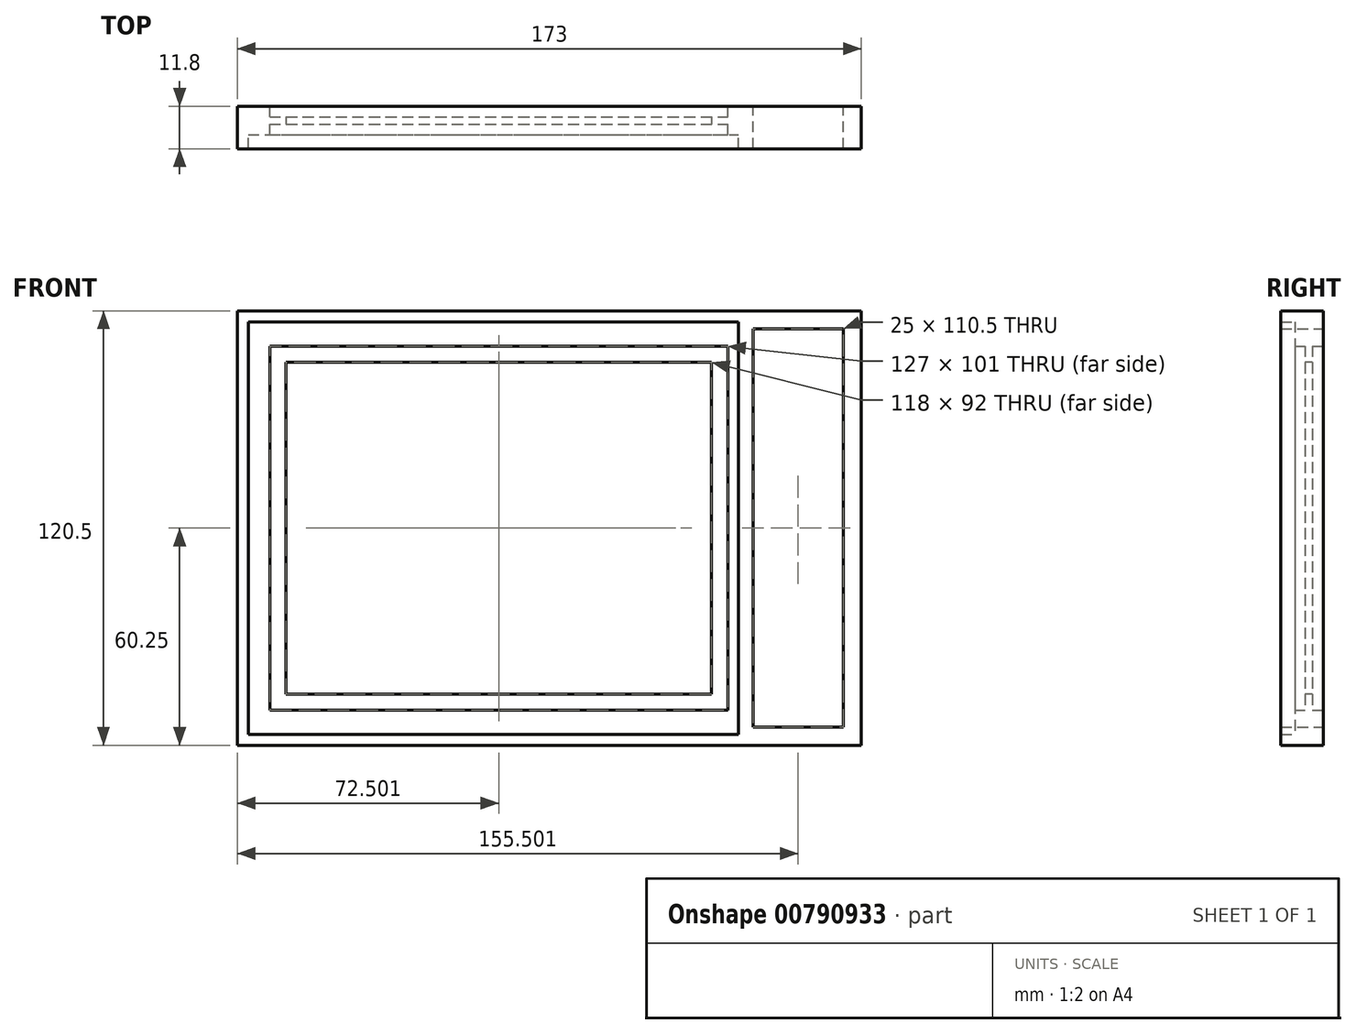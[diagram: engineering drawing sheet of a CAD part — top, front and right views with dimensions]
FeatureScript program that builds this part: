
annotation { "Feature Type Name" : "Feature", "Feature Type Description" : "" }
export const myFeature = defineFeature(function(context is Context, id is Id, definition is map)
    precondition{}
    {
        {
            var Q0;
            Q0=qCreatedBy(makeId("Front.planeOp"),FACE);
            var sketch = newSketch(context, id + "F0", { "sketchPlane" : qUnion([Q0])});
            skLineSegment(sketch, "E0.bottom", {"start": v(-104.32, 60.25) * mm, "end": v(68.68, 60.25) * mm});
            skLineSegment(sketch, "E0.top", {"start": v(-104.32, -60.25) * mm, "end": v(68.68, -60.25) * mm});
            skLineSegment(sketch, "E0.left", {"start": v(-104.32, 60.25) * mm, "end": v(-104.32, -60.25) * mm});
            skLineSegment(sketch, "E0.right", {"start": v(68.68, 60.25) * mm, "end": v(68.68, -60.25) * mm});
            skLineSegment(sketch, "E1.bottom", {"start": v(-95.32, 50.5) * mm, "end": v(31.68, 50.5) * mm});
            skLineSegment(sketch, "E1.top", {"start": v(-95.32, -50.5) * mm, "end": v(31.68, -50.5) * mm});
            skLineSegment(sketch, "E1.left", {"start": v(-95.32, 50.5) * mm, "end": v(-95.32, -50.5) * mm});
            skLineSegment(sketch, "E1.right", {"start": v(31.68, 50.5) * mm, "end": v(31.68, -50.5) * mm});
            skLineSegment(sketch, "E2.bottom", {"start": v(38.68, 55.25) * mm, "end": v(63.68, 55.25) * mm});
            skLineSegment(sketch, "E2.top", {"start": v(38.68, -55.25) * mm, "end": v(63.68, -55.25) * mm});
            skLineSegment(sketch, "E2.left", {"start": v(38.68, 55.25) * mm, "end": v(38.68, -55.25) * mm});
            skLineSegment(sketch, "E2.right", {"start": v(63.68, 55.25) * mm, "end": v(63.68, -55.25) * mm});
            skLineSegment(sketch, "E3.bottom", {"start": v(-90.82, 46) * mm, "end": v(27.18, 46) * mm});
            skLineSegment(sketch, "E3.top", {"start": v(-90.82, -46) * mm, "end": v(27.18, -46) * mm});
            skLineSegment(sketch, "E3.left", {"start": v(-90.82, 46) * mm, "end": v(-90.82, -46) * mm});
            skLineSegment(sketch, "E3.right", {"start": v(27.18, 46) * mm, "end": v(27.18, -46) * mm});
            skLineSegment(sketch, "E4.bottom", {"start": v(-101.32, 57.25) * mm, "end": v(34.68, 57.25) * mm});
            skLineSegment(sketch, "E4.top", {"start": v(-101.32, -57.25) * mm, "end": v(34.68, -57.25) * mm});
            skLineSegment(sketch, "E4.left", {"start": v(-101.32, 57.25) * mm, "end": v(-101.32, -57.25) * mm});
            skLineSegment(sketch, "E4.right", {"start": v(34.68, 57.25) * mm, "end": v(34.68, -57.25) * mm});
            skSolve(sketch);
        }
        {
            var Q0;
            Q0=qSketchRegion(id+"F0",true);
            var Q1;
            Q1=makeQuery(id+"F0.imprint","IMPRINT",FACE,{"disambiguationData":[TD([[makeQuery(id+"F0.imprint","IMPRINT",EDGE,{"derivedFrom":sQuery(id+"F0.wireOp",EDGE,"E1.bottom")}),1.0]])]});
            extrude(context, id + "F1", {"entities" : qUnion([Q0, Q1]), "depth" : 5.9 * mm, "offsetDistance" : 25 * mm});
        }
        {
            var Q0;
            Q0=makeQuery(id+"F1.opExtrude","SWEPT_BODY",BODY,{"disambiguationData":[OSD([sQuery(id+"F0.wireOp",EDGE,"E0.bottom"),sQuery(id+"F0.wireOp",EDGE,"E0.top"),sQuery(id+"F0.wireOp",EDGE,"E0.left"),sQuery(id+"F0.wireOp",EDGE,"E0.right"),sQuery(id+"F0.wireOp",EDGE,"E1.bottom"),sQuery(id+"F0.wireOp",EDGE,"E1.top"),sQuery(id+"F0.wireOp",EDGE,"E1.left"),sQuery(id+"F0.wireOp",EDGE,"E1.right"),sQuery(id+"F0.wireOp",EDGE,"E2.top"),sQuery(id+"F0.wireOp",EDGE,"E2.left"),sQuery(id+"F0.wireOp",EDGE,"E2.right")])]});
            var Q1;
            Q1=makeQuery(id+"F1.opExtrude","CAP_FACE",FACE,{"disambiguationData":[OSD([sQuery(id+"F0.wireOp",EDGE,"E0.bottom"),sQuery(id+"F0.wireOp",EDGE,"E0.top"),sQuery(id+"F0.wireOp",EDGE,"E0.left"),sQuery(id+"F0.wireOp",EDGE,"E0.right"),sQuery(id+"F0.wireOp",EDGE,"E1.bottom"),sQuery(id+"F0.wireOp",EDGE,"E1.top"),sQuery(id+"F0.wireOp",EDGE,"E1.left"),sQuery(id+"F0.wireOp",EDGE,"E1.right"),sQuery(id+"F0.wireOp",EDGE,"E2.bottom"),sQuery(id+"F0.wireOp",EDGE,"E2.left"),sQuery(id+"F0.wireOp",EDGE,"E2.right")])],"isStart":true});
            mirror(context, id + "F2", {"operationType" : NewBodyOperationType.ADD, "entities" : qUnion([Q0]), "mirrorPlane" : qUnion([Q1])});
        }
        {
            var Q0;
            Q0=makeQuery(id+"F0.imprint","IMPRINT",FACE,{"disambiguationData":[TD([[makeQuery(id+"F0.imprint","IMPRINT",EDGE,{"derivedFrom":sQuery(id+"F0.wireOp",EDGE,"E1.bottom")}),-1.0]])]});
            var Q1;
            Q1=makeQuery(id+"F1.opExtrude","CAP_FACE",FACE,{"disambiguationData":[OSD([sQuery(id+"F0.wireOp",EDGE,"E0.bottom"),sQuery(id+"F0.wireOp",EDGE,"E0.top"),sQuery(id+"F0.wireOp",EDGE,"E0.left"),sQuery(id+"F0.wireOp",EDGE,"E0.right"),sQuery(id+"F0.wireOp",EDGE,"E1.bottom"),sQuery(id+"F0.wireOp",EDGE,"E1.top"),sQuery(id+"F0.wireOp",EDGE,"E1.left"),sQuery(id+"F0.wireOp",EDGE,"E1.right"),sQuery(id+"F0.wireOp",EDGE,"E2.bottom"),sQuery(id+"F0.wireOp",EDGE,"E2.left"),sQuery(id+"F0.wireOp",EDGE,"E2.right")])],"isStart":false});
            extrude(context, id + "F3", {"entities" : qUnion([Q0, Q1]), "operationType" : NewBodyOperationType.ADD, "oppositeDirection" : true, "depth" : 2.9 * mm, "offsetDistance" : 25 * mm, "hasSecondDirection" : true, "secondDirectionOppositeDirection" : true, "secondDirectionDepth" : 0.9 * mm});
        }
        {
            var Q0;
            Q0=makeQuery(id+"F0.imprint","IMPRINT",FACE,{"disambiguationData":[TD([[makeQuery(id+"F0.imprint","IMPRINT",EDGE,{"derivedFrom":sQuery(id+"F0.wireOp",EDGE,"E1.bottom")}),1.0]])]});
            extrude(context, id + "F4", {"entities" : qUnion([Q0]), "operationType" : NewBodyOperationType.REMOVE, "depth" : 6 * mm, "offsetDistance" : 25 * mm, "hasSecondDirection" : true, "secondDirectionOppositeDirection" : false, "secondDirectionDepth" : 2 * mm});
        }
    });
